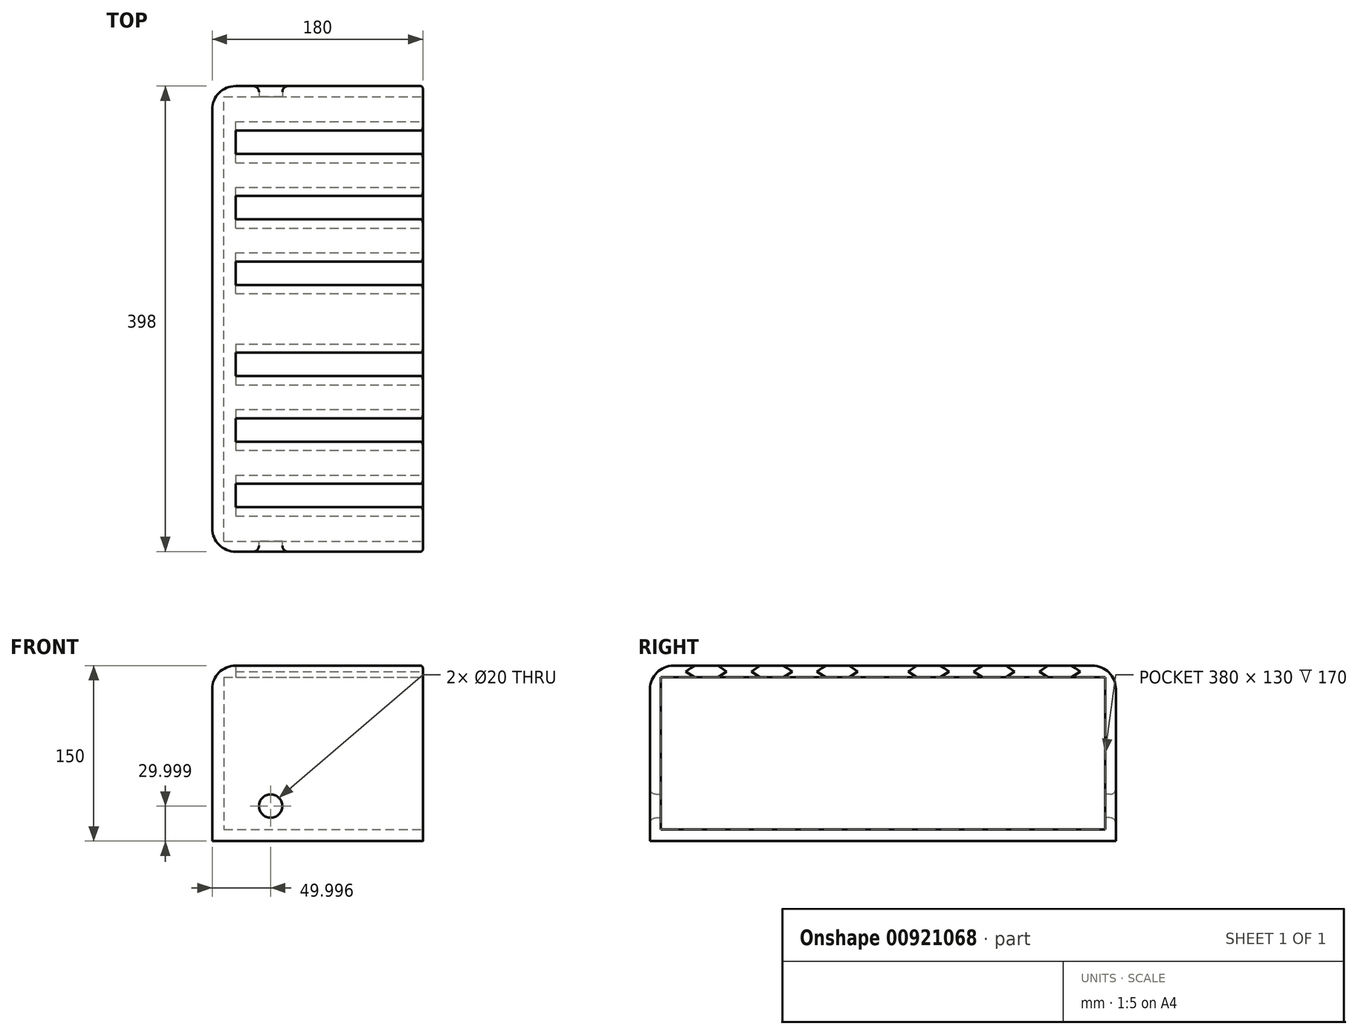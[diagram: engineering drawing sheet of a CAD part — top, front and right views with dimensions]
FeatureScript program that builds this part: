
annotation { "Feature Type Name" : "Feature", "Feature Type Description" : "" }
export const myFeature = defineFeature(function(context is Context, id is Id, definition is map)
    precondition{}
    {
        {
            var Q0;
            Q0=qCreatedBy(makeId("Front.planeOp"),FACE);
            var sketch = newSketch(context, id + "F0", { "sketchPlane" : qUnion([Q0])});
            skLineSegment(sketch, "E0.bottom", {"start": v(-139.04, 79.12) * mm, "end": v(40.96, 79.12) * mm});
            skLineSegment(sketch, "E0.top", {"start": v(-139.04, -70.88) * mm, "end": v(40.96, -70.88) * mm});
            skLineSegment(sketch, "E0.left", {"start": v(-139.04, 79.12) * mm, "end": v(-139.04, -70.88) * mm});
            skLineSegment(sketch, "E0.right", {"start": v(40.96, 79.12) * mm, "end": v(40.96, -70.88) * mm});
            skSolve(sketch);
        }
        {
            var Q0;
            Q0=makeQuery(id+"F0.imprint","IMPRINT",FACE,{"disambiguationData":[TD([[makeQuery(id+"F0.imprint","IMPRINT",EDGE,{"derivedFrom":sQuery(id+"F0.wireOp",EDGE,"E0.bottom")}),-1.0]])]});
            extrude(context, id + "F1", {"entities" : qUnion([Q0]), "depth" : 199 * mm, "offsetDistance" : 25 * mm});
        }
        {
            var Q0;
            Q0=makeQuery(id+"F1.opExtrude","CAP_EDGE",EDGE,{"disambiguationData":[OSD([sQuery(id+"F0.wireOp",EDGE,"E0.bottom")])],"isStart":false});
            fillet(context, id + "F2", {"entities" : qUnion([Q0]), "radius" : 20 * mm, "tangentPropagation" : true, "allowEdgeOverflow" : false});
        }
        {
            var Q0;
            Q0=makeQuery(id+"F1.opExtrude","SWEPT_EDGE",EDGE,{"disambiguationData":[OSD([sQuery(id+"F0.wireOp",EDGE,"E0.bottom"),sQuery(id+"F0.wireOp",EDGE,"E0.left")])]});
            fillet(context, id + "F3", {"entities" : qUnion([Q0]), "radius" : 20 * mm, "tangentPropagation" : true, "allowEdgeOverflow" : false});
        }
        {
            var Q0;
            Q0=qCreatedBy(makeId("Front.planeOp"),FACE);
            var sketch = newSketch(context, id + "F4", { "sketchPlane" : qUnion([Q0])});
            skLineSegment(sketch, "E1", {"start": v(-129.04, 69.12) * mm, "end": v(-129.04, -60.88) * mm});
            skLineSegment(sketch, "E2", {"start": v(-129.04, -60.88) * mm, "end": v(258.15, -60.88) * mm});
            skLineSegment(sketch, "E3", {"start": v(258.15, -60.88) * mm, "end": v(258.15, 69.12) * mm});
            skLineSegment(sketch, "E4", {"start": v(-129.04, 69.12) * mm, "end": v(258.15, 69.12) * mm});
            skPoint(sketch, "E5.visualSharp", {"position": v(-129.04, 69.12) * mm});
            skPoint(sketch, "E6", {"position": v(40.8, 69.12) * mm});
            skSolve(sketch);
        }
        {
            var Q0;
            Q0=makeQuery(id+"F4.imprint","IMPRINT",FACE,{"disambiguationData":[TD([[makeQuery(id+"F4.imprint","IMPRINT",EDGE,{"derivedFrom":sQuery(id+"F4.wireOp",EDGE,"E1")}),1.0]])]});
            extrude(context, id + "F5", {"entities" : qUnion([Q0]), "operationType" : NewBodyOperationType.REMOVE, "depth" : 190 * mm, "offsetDistance" : 25 * mm});
        }
        {
            var Q0;
            Q0=makeQuery(id+"F1.opExtrude","SWEPT_FACE",FACE,{"disambiguationData":[OSD([sQuery(id+"F0.wireOp",EDGE,"E0.right")])]});
            var sketch = newSketch(context, id + "F6", { "sketchPlane" : qUnion([Q0])});
            skLineSegment(sketch, "E7", {"start": v(-104.98, 79.12) * mm, "end": v(-84.98, 79.12) * mm});
            skLineSegment(sketch, "E8", {"start": v(-104.98, 69.12) * mm, "end": v(-84.98, 69.12) * mm});
            skLineSegment(sketch, "E9", {"start": v(-104.98, 79.12) * mm, "end": v(-112.47, 74.12) * mm});
            skLineSegment(sketch, "E10", {"start": v(-112.47, 74.12) * mm, "end": v(-104.98, 69.12) * mm});
            skLineSegment(sketch, "E11", {"start": v(-84.98, 79.12) * mm, "end": v(-77.5, 74.12) * mm});
            skLineSegment(sketch, "E12", {"start": v(-77.5, 74.12) * mm, "end": v(-84.98, 69.12) * mm});
            skLineSegment(sketch, "E13", {"start": v(-104.98, 79.12) * mm, "end": v(-104.98, 109.12) * mm});
            skLineSegment(sketch, "E14", {"start": v(-84.98, 79.12) * mm, "end": v(-84.98, 104.12) * mm});
            skLineSegment(sketch, "E15", {"start": v(-84.98, 104.12) * mm, "end": v(-104.98, 109.12) * mm});
            skPoint(sketch, "E16", {"position": v(-87.98, 104.87) * mm});
            skPoint(sketch, "E17", {"position": v(-99.98, 107.87) * mm});
            skLineSegment(sketch, "E18", {"start": v(-87.98, 104.87) * mm, "end": v(-76.58, 150.47) * mm});
            skPoint(sketch, "E19", {"position": v(-84.98, 84.12) * mm});
            skLineSegment(sketch, "E20", {"start": v(-84.98, 84.12) * mm, "end": v(-68.88, 148.54) * mm});
            skLineSegment(sketch, "E21", {"start": v(-72.95, 152.65) * mm, "end": v(-71.06, 152.18) * mm});
            skLineSegment(sketch, "E22", {"start": v(-99.98, 107.87) * mm, "end": v(-98.4, 114.17) * mm});
            skLineSegment(sketch, "E23", {"start": v(-99.5, 116) * mm, "end": v(-101.47, 116.49) * mm});
            skLineSegment(sketch, "E24", {"start": v(-104.98, 109.12) * mm, "end": v(-103.28, 115.42) * mm});
            skPoint(sketch, "E25.visualSharp", {"position": v(-68.15, 151.45) * mm});
            skArc(sketch, "E25.filletArc", {"start": v(-68.88, 148.54) * mm, "mid": v(-69.22, 150.81) * mm, "end": v(-71.06, 152.18) * mm});
            skPoint(sketch, "E26.visualSharp", {"position": v(-75.86, 153.38) * mm});
            skArc(sketch, "E26.filletArc", {"start": v(-72.95, 152.65) * mm, "mid": v(-75.22, 152.31) * mm, "end": v(-76.58, 150.47) * mm});
            skPoint(sketch, "E27.visualSharp", {"position": v(-102.9, 116.84) * mm});
            skArc(sketch, "E27.filletArc", {"start": v(-101.47, 116.49) * mm, "mid": v(-102.59, 116.32) * mm, "end": v(-103.28, 115.42) * mm});
            skPoint(sketch, "E28.visualSharp", {"position": v(-98.04, 115.63) * mm});
            skArc(sketch, "E28.filletArc", {"start": v(-98.4, 114.17) * mm, "mid": v(-98.58, 115.31) * mm, "end": v(-99.5, 116) * mm});
            skLineSegment(sketch, "E29", {"start": v(-48.98, 79.12) * mm, "end": v(-28.98, 79.12) * mm});
            skLineSegment(sketch, "E30", {"start": v(-48.98, 69.12) * mm, "end": v(-28.98, 69.12) * mm});
            skLineSegment(sketch, "E31", {"start": v(-48.98, 79.12) * mm, "end": v(-56.47, 74.12) * mm});
            skLineSegment(sketch, "E32", {"start": v(-56.47, 74.12) * mm, "end": v(-48.98, 69.12) * mm});
            skLineSegment(sketch, "E33", {"start": v(-28.98, 79.12) * mm, "end": v(-21.5, 74.12) * mm});
            skLineSegment(sketch, "E34", {"start": v(-21.5, 74.12) * mm, "end": v(-28.98, 69.12) * mm});
            skLineSegment(sketch, "E35", {"start": v(-48.98, 79.12) * mm, "end": v(-48.98, 109.12) * mm});
            skLineSegment(sketch, "E36", {"start": v(-28.98, 79.12) * mm, "end": v(-28.98, 104.12) * mm});
            skLineSegment(sketch, "E37", {"start": v(-28.98, 104.12) * mm, "end": v(-48.98, 109.12) * mm});
            skPoint(sketch, "E38", {"position": v(-31.98, 104.87) * mm});
            skPoint(sketch, "E39", {"position": v(-43.98, 107.87) * mm});
            skLineSegment(sketch, "E40", {"start": v(-31.98, 104.87) * mm, "end": v(-20.58, 150.47) * mm});
            skPoint(sketch, "E41", {"position": v(-28.98, 84.12) * mm});
            skLineSegment(sketch, "E42", {"start": v(-28.98, 84.12) * mm, "end": v(-12.88, 148.54) * mm});
            skLineSegment(sketch, "E43", {"start": v(-16.95, 152.65) * mm, "end": v(-15.06, 152.18) * mm});
            skLineSegment(sketch, "E44", {"start": v(-43.98, 107.87) * mm, "end": v(-42.4, 114.17) * mm});
            skLineSegment(sketch, "E45", {"start": v(-43.5, 116) * mm, "end": v(-45.47, 116.49) * mm});
            skLineSegment(sketch, "E46", {"start": v(-48.98, 109.12) * mm, "end": v(-47.28, 115.42) * mm});
            skPoint(sketch, "E47.visualSharp", {"position": v(-12.15, 151.45) * mm});
            skArc(sketch, "E47.filletArc", {"start": v(-12.88, 148.54) * mm, "mid": v(-13.22, 150.81) * mm, "end": v(-15.06, 152.18) * mm});
            skPoint(sketch, "E48.visualSharp", {"position": v(-19.86, 153.38) * mm});
            skArc(sketch, "E48.filletArc", {"start": v(-16.95, 152.65) * mm, "mid": v(-19.22, 152.31) * mm, "end": v(-20.58, 150.47) * mm});
            skPoint(sketch, "E49.visualSharp", {"position": v(-46.9, 116.84) * mm});
            skArc(sketch, "E49.filletArc", {"start": v(-45.47, 116.49) * mm, "mid": v(-46.59, 116.32) * mm, "end": v(-47.28, 115.42) * mm});
            skPoint(sketch, "E50.visualSharp", {"position": v(-42.04, 115.63) * mm});
            skArc(sketch, "E50.filletArc", {"start": v(-42.4, 114.17) * mm, "mid": v(-42.58, 115.31) * mm, "end": v(-43.5, 116) * mm});
            skLineSegment(sketch, "E51", {"start": v(-161.02, 79.12) * mm, "end": v(-141.02, 79.12) * mm});
            skLineSegment(sketch, "E52", {"start": v(-161.02, 69.12) * mm, "end": v(-141.02, 69.12) * mm});
            skLineSegment(sketch, "E53", {"start": v(-161.02, 79.12) * mm, "end": v(-168.5, 74.12) * mm});
            skLineSegment(sketch, "E54", {"start": v(-168.5, 74.12) * mm, "end": v(-161.02, 69.12) * mm});
            skLineSegment(sketch, "E55", {"start": v(-141.02, 79.12) * mm, "end": v(-133.53, 74.12) * mm});
            skLineSegment(sketch, "E56", {"start": v(-133.53, 74.12) * mm, "end": v(-141.02, 69.12) * mm});
            skLineSegment(sketch, "E57", {"start": v(-161.02, 79.12) * mm, "end": v(-161.02, 109.12) * mm});
            skLineSegment(sketch, "E58", {"start": v(-141.02, 79.12) * mm, "end": v(-141.02, 104.12) * mm});
            skLineSegment(sketch, "E59", {"start": v(-141.02, 104.12) * mm, "end": v(-161.02, 109.12) * mm});
            skPoint(sketch, "E60", {"position": v(-144.02, 104.87) * mm});
            skPoint(sketch, "E61", {"position": v(-156.02, 107.87) * mm});
            skLineSegment(sketch, "E62", {"start": v(-144.02, 104.87) * mm, "end": v(-132.62, 150.47) * mm});
            skPoint(sketch, "E63", {"position": v(-141.02, 84.12) * mm});
            skLineSegment(sketch, "E64", {"start": v(-141.02, 84.12) * mm, "end": v(-124.91, 148.54) * mm});
            skLineSegment(sketch, "E65", {"start": v(-128.98, 152.65) * mm, "end": v(-127.1, 152.18) * mm});
            skLineSegment(sketch, "E66", {"start": v(-156.02, 107.87) * mm, "end": v(-154.44, 114.17) * mm});
            skLineSegment(sketch, "E67", {"start": v(-155.53, 116) * mm, "end": v(-157.5, 116.49) * mm});
            skLineSegment(sketch, "E68", {"start": v(-161.02, 109.12) * mm, "end": v(-159.31, 115.42) * mm});
            skPoint(sketch, "E69.visualSharp", {"position": v(-124.18, 151.45) * mm});
            skArc(sketch, "E69.filletArc", {"start": v(-124.91, 148.54) * mm, "mid": v(-125.25, 150.81) * mm, "end": v(-127.1, 152.18) * mm});
            skPoint(sketch, "E70.visualSharp", {"position": v(-131.89, 153.38) * mm});
            skArc(sketch, "E70.filletArc", {"start": v(-128.98, 152.65) * mm, "mid": v(-131.25, 152.31) * mm, "end": v(-132.62, 150.47) * mm});
            skPoint(sketch, "E71.visualSharp", {"position": v(-158.93, 116.84) * mm});
            skArc(sketch, "E71.filletArc", {"start": v(-157.5, 116.49) * mm, "mid": v(-158.62, 116.32) * mm, "end": v(-159.31, 115.42) * mm});
            skPoint(sketch, "E72.visualSharp", {"position": v(-154.08, 115.63) * mm});
            skArc(sketch, "E72.filletArc", {"start": v(-154.44, 114.17) * mm, "mid": v(-154.6, 115.31) * mm, "end": v(-155.53, 116) * mm});
            skSolve(sketch);
        }
        {
            var Q0;
            Q0=makeQuery(id+"F6.imprint","IMPRINT",FACE,{"disambiguationData":[TD([[makeQuery(id+"F6.imprint","IMPRINT",EDGE,{"derivedFrom":sQuery(id+"F6.wireOp",EDGE,"E51")}),-1.0]])]});
            var Q1;
            Q1=makeQuery(id+"F6.imprint","IMPRINT",FACE,{"disambiguationData":[TD([[makeQuery(id+"F6.imprint","IMPRINT",EDGE,{"derivedFrom":sQuery(id+"F6.wireOp",EDGE,"E7")}),-1.0]])]});
            var Q2;
            Q2=makeQuery(id+"F6.imprint","IMPRINT",FACE,{"disambiguationData":[TD([[makeQuery(id+"F6.imprint","IMPRINT",EDGE,{"derivedFrom":sQuery(id+"F6.wireOp",EDGE,"E29")}),-1.0]])]});
            extrude(context, id + "F7", {"entities" : qUnion([Q0, Q1, Q2]), "operationType" : NewBodyOperationType.REMOVE, "oppositeDirection" : true, "depth" : 160 * mm, "offsetDistance" : 25 * mm});
        }
        {
            var Q0;
            Q0=qCreatedBy(makeId("Front.planeOp"),FACE);
            var sketch = newSketch(context, id + "F8", { "sketchPlane" : qUnion([Q0])});
            skCircle(sketch, "E73", {"center": v(-89.04, -40.88) * mm, "radius": 10 * mm});
            skSolve(sketch);
        }
        {
            var Q0;
            Q0=makeQuery(id+"F8.imprint","IMPRINT",FACE,{"disambiguationData":[TD([[makeQuery(id+"F8.imprint","IMPRINT",EDGE,{"derivedFrom":sQuery(id+"F8.wireOp",EDGE,"E73")}),1.0]])]});
            extrude(context, id + "F9", {"entities" : qUnion([Q0]), "operationType" : NewBodyOperationType.REMOVE, "depth" : 264.3 * mm, "offsetDistance" : 25 * mm});
        }
        {
            var Q0;
            Q0=makeQuery(id+"F1.opExtrude","CAP_EDGE",EDGE,{"disambiguationData":[OSD([sQuery(id+"F0.wireOp",EDGE,"E0.right")])],"isStart":false});
            var Q1;
            Q1=makeQuery(id+"F2.opFillet","BLEND_EDGE",EDGE,{"blendedFrom":[makeQuery(id+"F1.opExtrude","CAP_EDGE",EDGE,{"disambiguationData":[OSD([sQuery(id+"F0.wireOp",EDGE,"E0.bottom")])],"isStart":false}),makeQuery(id+"F1.opExtrude","SWEPT_FACE",FACE,{"disambiguationData":[OSD([sQuery(id+"F0.wireOp",EDGE,"E0.right")])]})],"blendedInto":[makeQuery(id+"F1.opExtrude","SWEPT_FACE",FACE,{"disambiguationData":[OSD([sQuery(id+"F0.wireOp",EDGE,"E0.right")])]})]});
            var Q2;
            {var subQ0=sQuery(id+"F0.wireOp",EDGE,"E0.bottom");var subQ1=sQuery(id+"F0.wireOp",EDGE,"E0.right");Q2=makeQuery(id+"F7.boolean.opBoolean","SPLIT",EDGE,{"disambiguationData":[TD([makeQuery(id+"F7.opExtrude","SWEPT_FACE",FACE,{"disambiguationData":[OSD([sQuery(id+"F6.wireOp",EDGE,"E9")])]})])],"derivedFrom":makeQuery(id+"F1.opExtrude","SWEPT_EDGE",EDGE,{"disambiguationData":[OSD([subQ0,subQ1])]})});}
            var Q3;
            {var subQ0=sQuery(id+"F0.wireOp",EDGE,"E0.bottom");var subQ1=sQuery(id+"F0.wireOp",EDGE,"E0.right");Q3=makeQuery(id+"F7.boolean.opBoolean","SPLIT",EDGE,{"disambiguationData":[TD([makeQuery(id+"F7.opExtrude","SWEPT_FACE",FACE,{"disambiguationData":[OSD([sQuery(id+"F6.wireOp",EDGE,"E11")])]})])],"derivedFrom":makeQuery(id+"F1.opExtrude","SWEPT_EDGE",EDGE,{"disambiguationData":[OSD([subQ0,subQ1])]})});}
            var Q4;
            {var subQ0=sQuery(id+"F0.wireOp",EDGE,"E0.bottom");var subQ1=sQuery(id+"F0.wireOp",EDGE,"E0.right");Q4=makeQuery(id+"F7.boolean.opBoolean","SPLIT",EDGE,{"disambiguationData":[TD([makeQuery(id+"F7.opExtrude","SWEPT_FACE",FACE,{"disambiguationData":[OSD([sQuery(id+"F6.wireOp",EDGE,"E33")])]})])],"derivedFrom":makeQuery(id+"F1.opExtrude","SWEPT_EDGE",EDGE,{"disambiguationData":[OSD([subQ0,subQ1])]})});}
            fillet(context, id + "F10", {"entities" : qUnion([Q0, Q1, Q2, Q3, Q4]), "radius" : 2 * mm, "tangentPropagation" : true, "allowEdgeOverflow" : false});
        }
        {
            var Q0;
            Q0=makeQuery(id+"F9.boolean.opBoolean","INTERSECT",EDGE,{"derivedFrom":[makeQuery(id+"F1.opExtrude","CAP_FACE",FACE,{"disambiguationData":[OSD([sQuery(id+"F0.wireOp",EDGE,"E0.bottom"),sQuery(id+"F0.wireOp",EDGE,"E0.top"),sQuery(id+"F0.wireOp",EDGE,"E0.left"),sQuery(id+"F0.wireOp",EDGE,"E0.right")])],"isStart":false}),makeQuery(id+"F9.opExtrude","SWEPT_FACE",FACE,{"disambiguationData":[OSD([sQuery(id+"F8.wireOp",EDGE,"E73")])]})]});
            fillet(context, id + "F11", {"entities" : qUnion([Q0]), "radius" : 5 * mm, "tangentPropagation" : true, "allowEdgeOverflow" : false});
        }
        {
            var Q0;
            Q0=makeQuery(id+"F1.opExtrude","SWEPT_BODY",BODY,{"disambiguationData":[OSD([sQuery(id+"F0.wireOp",EDGE,"E0.bottom"),sQuery(id+"F0.wireOp",EDGE,"E0.top"),sQuery(id+"F0.wireOp",EDGE,"E0.left"),sQuery(id+"F0.wireOp",EDGE,"E0.right")])]});
            var Q1;
            Q1=qCreatedBy(makeId("Front.planeOp"),FACE);
            mirror(context, id + "F12", {"operationType" : NewBodyOperationType.ADD, "entities" : qUnion([Q0]), "mirrorPlane" : qUnion([Q1])});
        }
    });
